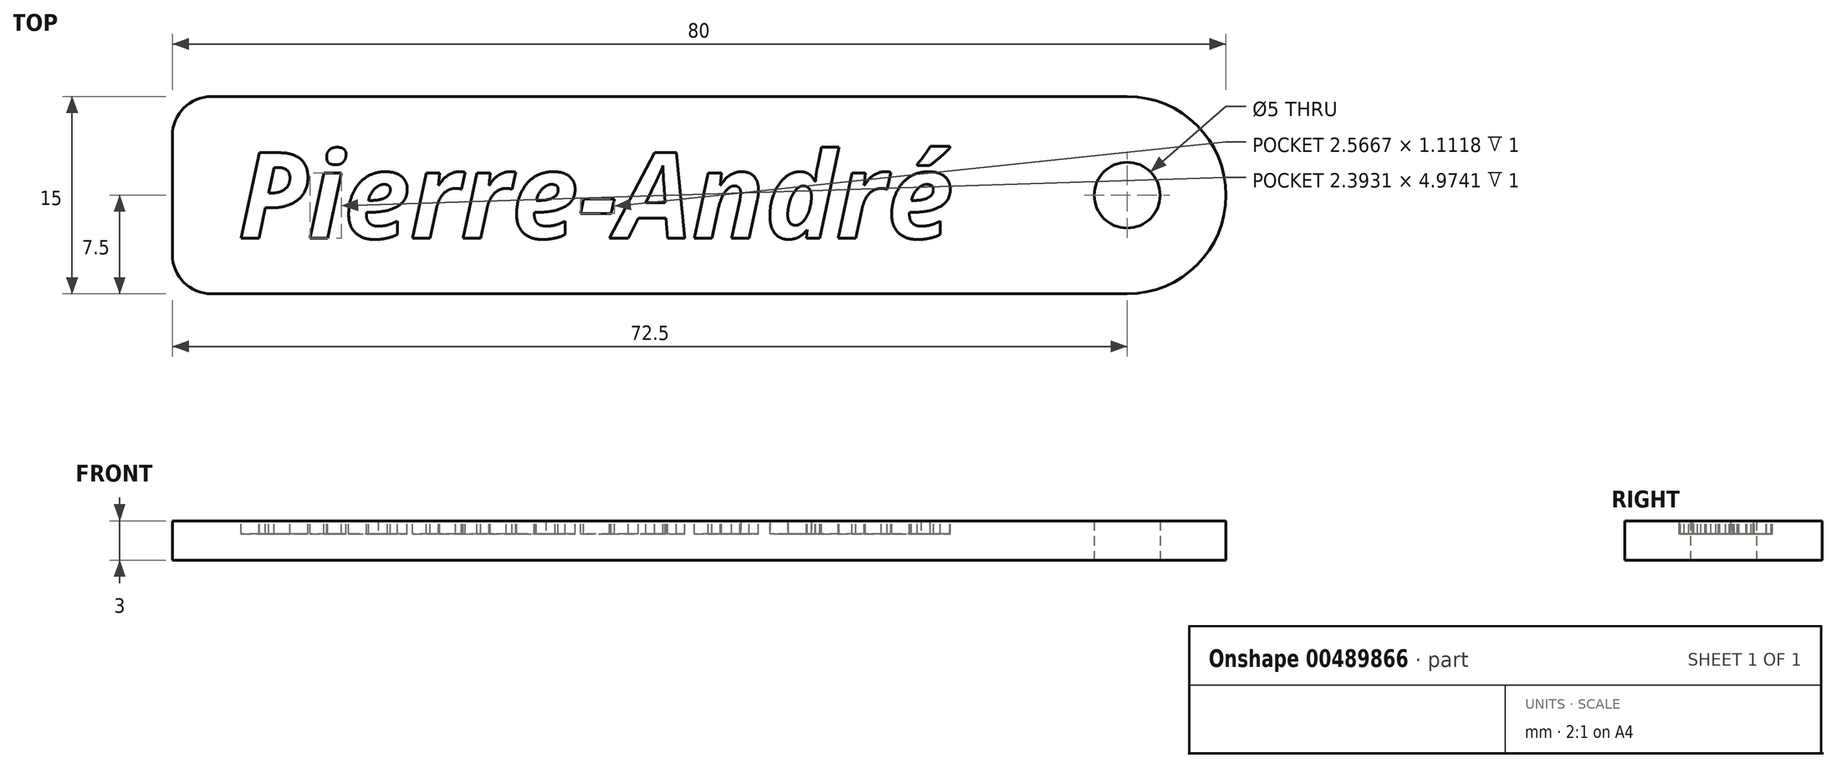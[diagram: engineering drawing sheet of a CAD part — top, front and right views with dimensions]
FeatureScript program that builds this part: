
annotation { "Feature Type Name" : "Feature", "Feature Type Description" : "" }
export const myFeature = defineFeature(function(context is Context, id is Id, definition is map)
    precondition{}
    {
        {
            var Q0;
            Q0=qCreatedBy(makeId("Top.planeOp"),FACE);
            var sketch = newSketch(context, id + "F0", { "sketchPlane" : qUnion([Q0])});
            skLineSegment(sketch, "E0.bottom", {"start": v(-37, 7.5) * mm, "end": v(32.5, 7.5) * mm});
            skLineSegment(sketch, "E0.top", {"start": v(-37, -7.5) * mm, "end": v(32.5, -7.5) * mm});
            skLineSegment(sketch, "E0.left", {"start": v(-40, 4.5) * mm, "end": v(-40, -4.5) * mm});
            skArc(sketch, "E1", {"start": v(32.5, -7.5) * mm, "mid": v(40, 0) * mm, "end": v(32.5, 7.5) * mm});
            skCircle(sketch, "E2", {"center": v(32.5, 0) * mm, "radius": 2.5 * mm});
            skPoint(sketch, "E3.visualSharp", {"position": v(-40, 7.5) * mm});
            skArc(sketch, "E3.filletArc", {"start": v(-37, 7.5) * mm, "mid": v(-39.12, 6.62) * mm, "end": v(-40, 4.5) * mm});
            skPoint(sketch, "E4.visualSharp", {"position": v(-40, -7.5) * mm});
            skArc(sketch, "E4.filletArc", {"start": v(-40, -4.5) * mm, "mid": v(-39.12, -6.62) * mm, "end": v(-37, -7.5) * mm});
            skLineSegment(sketch, "E5", {"start": v(40, 42.5) * mm, "end": v(40, -42.11) * mm, "construction": true});
            skSolve(sketch);
        }
        {
            var Q0;
            Q0=makeQuery(id+"F0.imprint","IMPRINT",FACE,{"disambiguationData":[TD([[makeQuery(id+"F0.imprint","IMPRINT",EDGE,{"derivedFrom":sQuery(id+"F0.wireOp",EDGE,"E0.bottom")}),-1.0]])]});
            extrude(context, id + "F1", {"entities" : qUnion([Q0]), "depth" : 3 * mm});
        }
        {
            var Q0;
            Q0=makeQuery(id+"F1.opExtrude","CAP_FACE",FACE,{"disambiguationData":[OSD([sQuery(id+"F0.wireOp",EDGE,"E0.bottom"),sQuery(id+"F0.wireOp",EDGE,"E0.top"),sQuery(id+"F0.wireOp",EDGE,"E0.left"),sQuery(id+"F0.wireOp",EDGE,"E1"),sQuery(id+"F0.wireOp",EDGE,"E2"),sQuery(id+"F0.wireOp",EDGE,"E3.filletArc"),sQuery(id+"F0.wireOp",EDGE,"E4.filletArc")])],"isStart":false});
            var sketch = newSketch(context, id + "F2", { "sketchPlane" : qUnion([Q0])});
            skText(sketch, "E6", { "text": "Pierre-André", "fontName": "OpenSans-BoldItalic.ttf"});
            const initialGuessF2  = {"E6": [-0.035, -0.00328, 1, 0, 0.00656]};
            skSetInitialGuess(sketch, initialGuessF2);
            skSolve(sketch);
        }
        {
            var Q0;
            Q0=qSketchRegion(id+"F2",true);
            extrude(context, id + "F3", {"entities" : qUnion([Q0]), "operationType" : NewBodyOperationType.REMOVE, "oppositeDirection" : true, "depth" : 1 * mm});
        }
    });
